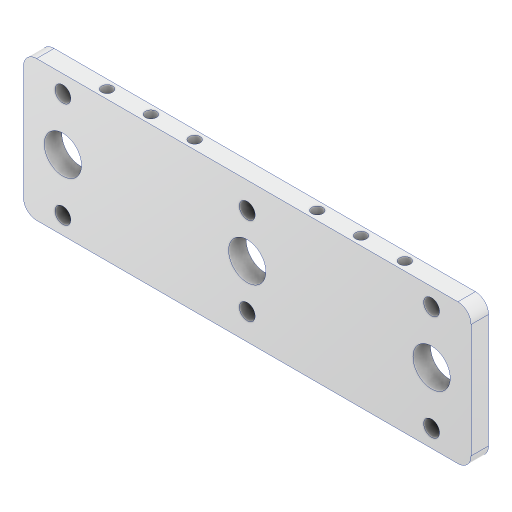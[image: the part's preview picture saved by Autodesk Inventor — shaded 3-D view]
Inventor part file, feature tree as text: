
AUTODESK INVENTOR PART (.ipt)
format: ipt  version: 2023.2 (Build 272271000, 271)  size: 285,696 bytes
history: native  units: mm
features: extrude x8, sketch x7, projected_geometry x5, fillet x2, other x1, mirror x1
ambient origin geometry x8: Origin, YZ Plane, XZ Plane, XY Plane, X Axis, Y Axis, Z Axis, Center Point
bodies: Body1 (feature_tree)
feature tree (24):
  other  "솔리드1"
  extrude  "돌출1"  Depth=96.2mm
  extrude  "돌출2"  Depth=30.0mm
  extrude  "돌출3"  Depth=4.0mm TaperAngle=0.0deg
  fillet  "모깎기1"  Radius=8.5mm
  extrude  "돌출4"  Depth=92.2mm
  fillet  "모깎기2"  Radius=26.0mm
  extrude  "돌출5"  Depth=8.5mm
  sketch  "스케치6"
  extrude  "돌출6"  Depth=15.0mm
  extrude  "돌출7"  Depth=15.0mm
  extrude  "돌출8"  Depth=6.0mm
  mirror  "미러1"
  sketch  "스케치1"
  sketch  "스케치2"
  projected_geometry  "투영된 루프1"
  sketch  "스케치3"
  projected_geometry  "투영된 루프2"
  sketch  "스케치4"
  projected_geometry  "투영된 루프3"
  sketch  "스케치5"
  projected_geometry  "투영된 루프4"
  sketch  "스케치8"
  projected_geometry  "투영된 루프6"
